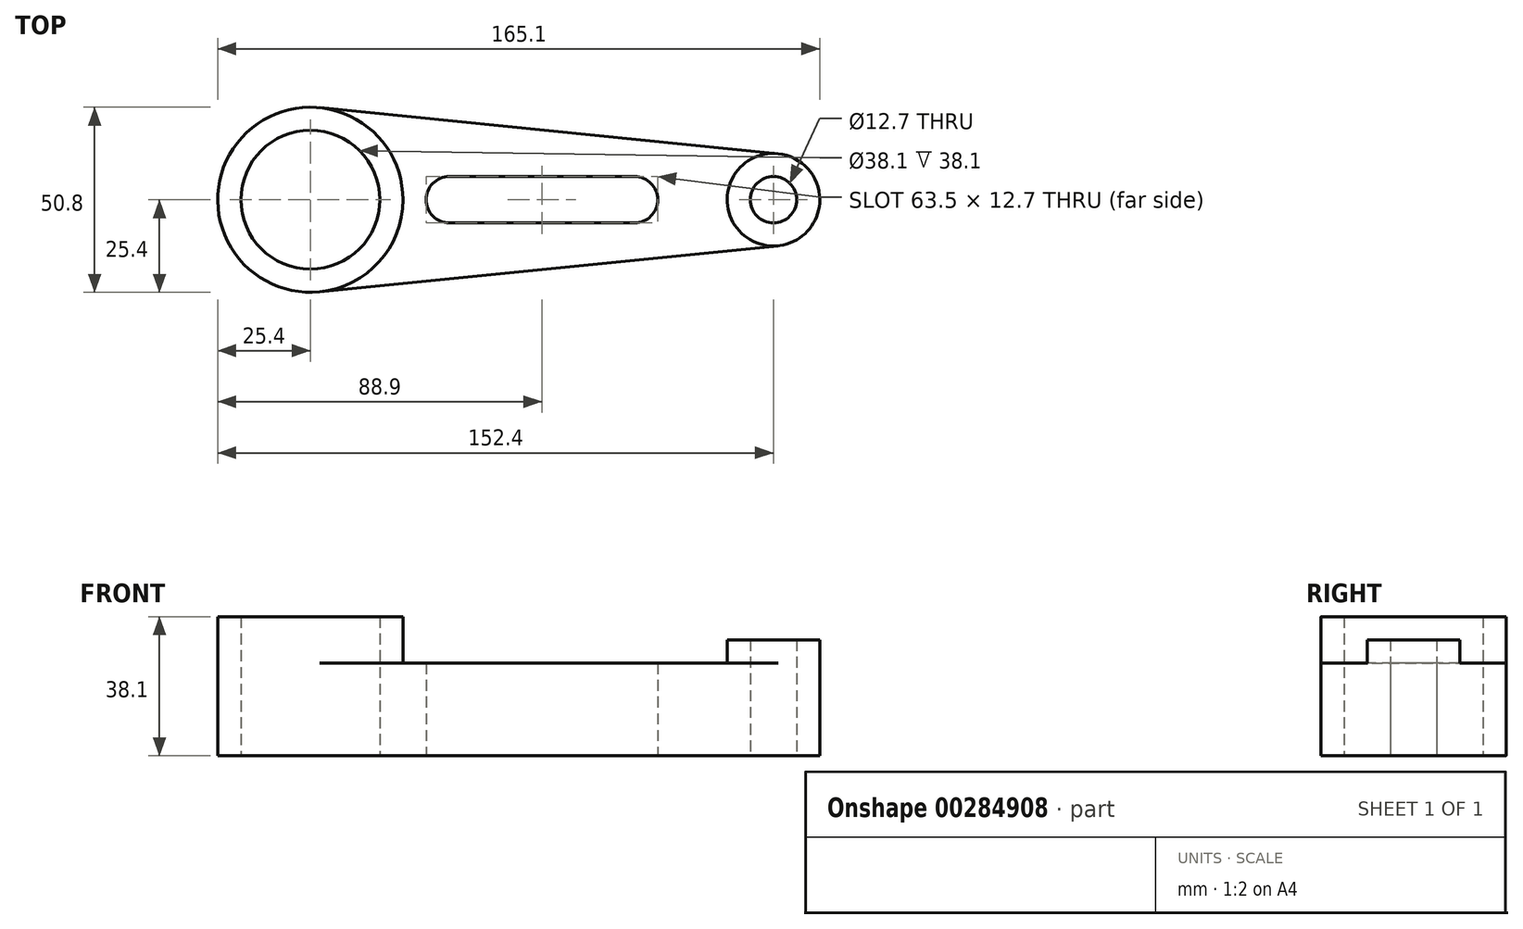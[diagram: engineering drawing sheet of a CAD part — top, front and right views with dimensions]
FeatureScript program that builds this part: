
annotation { "Feature Type Name" : "Feature", "Feature Type Description" : "" }
export const myFeature = defineFeature(function(context is Context, id is Id, definition is map)
    precondition{}
    {
        {
            var Q0;
            Q0=qCreatedBy(makeId("Top.planeOp"),FACE);
            var sketch = newSketch(context, id + "F0", { "sketchPlane" : qUnion([Q0])});
            skCircle(sketch, "E0", {"center": v(-38.1, 0) * mm, "radius": 25.4 * mm});
            skCircle(sketch, "E1", {"center": v(-38.1, 0) * mm, "radius": 19.05 * mm});
            skLineSegment(sketch, "E2", {"start": v(-35.56, 25.27) * mm, "end": v(90.17, 12.64) * mm});
            skLineSegment(sketch, "E3", {"start": v(-35.56, -25.27) * mm, "end": v(90.17, -12.64) * mm});
            skCircle(sketch, "E4", {"center": v(88.9, 0) * mm, "radius": 6.35 * mm});
            skCircle(sketch, "E5", {"center": v(88.9, 0) * mm, "radius": 12.7 * mm});
            skArc(sketch, "E6", {"start": v(0, 6.35) * mm, "mid": v(-6.35, 0) * mm, "end": v(0, -6.35) * mm});
            skArc(sketch, "E7", {"start": v(50.8, -6.35) * mm, "mid": v(57.15, 0) * mm, "end": v(50.8, 6.35) * mm});
            skLineSegment(sketch, "E8", {"start": v(0, 6.35) * mm, "end": v(50.8, 6.35) * mm});
            skLineSegment(sketch, "E9", {"start": v(0, -6.35) * mm, "end": v(50.8, -6.35) * mm});
            skSolve(sketch);
        }
        {
            var Q0;
            Q0 = qSketchRegion(id + "F0", true);
            extrude(context, id + "F1", {"entities" : qUnion([Q0]), "depth" : 25.4 * mm});
        }
        {
            var Q0;
            Q0=makeQuery(id+"F0.imprint","IMPRINT",FACE,{"disambiguationData":[TD([[makeQuery(id+"F0.imprint","IMPRINT",EDGE,{"derivedFrom":sQuery(id+"F0.wireOp",EDGE,"E1")}),-1.0]])]});
            extrude(context, id + "F2", {"entities" : qUnion([Q0]), "operationType" : NewBodyOperationType.ADD, "depth" : 38.1 * mm});
        }
        {
            var Q0;
            Q0=makeQuery(id+"F0.imprint","IMPRINT",FACE,{"disambiguationData":[TD([[makeQuery(id+"F0.imprint","IMPRINT",EDGE,{"derivedFrom":sQuery(id+"F0.wireOp",EDGE,"E4")}),-1.0]])]});
            extrude(context, id + "F3", {"entities" : qUnion([Q0]), "operationType" : NewBodyOperationType.ADD, "depth" : 31.75 * mm});
        }
    });
